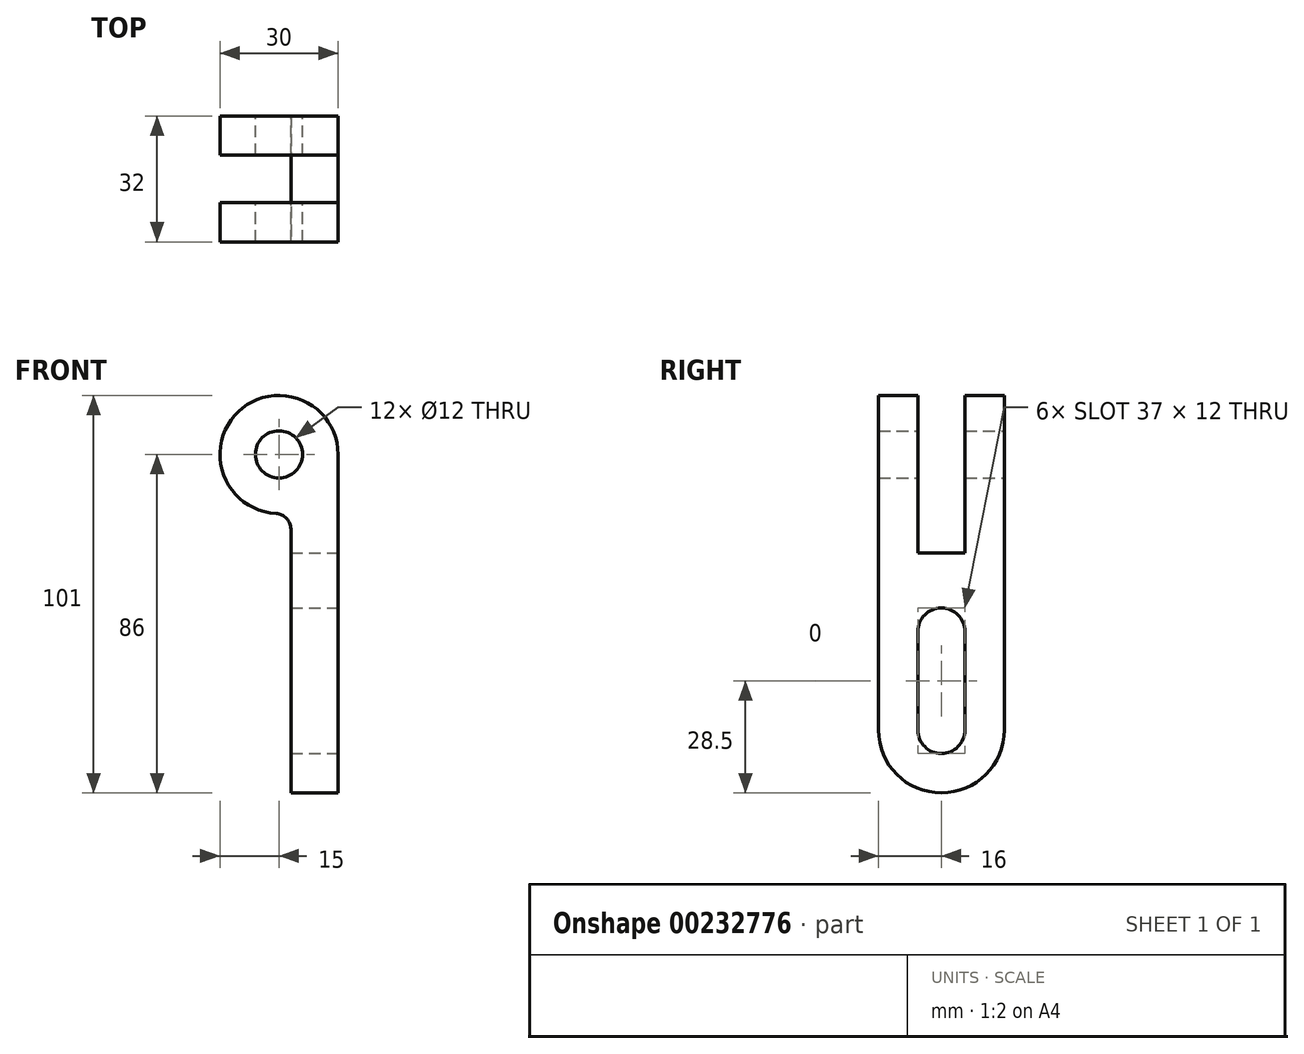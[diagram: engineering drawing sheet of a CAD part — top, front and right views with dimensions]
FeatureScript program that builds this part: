
annotation { "Feature Type Name" : "Feature", "Feature Type Description" : "" }
export const myFeature = defineFeature(function(context is Context, id is Id, definition is map)
    precondition{}
    {
        {
            var Q0;
            Q0=qCreatedBy(makeId("Front.planeOp"),FACE);
            var sketch = newSketch(context, id + "F0", { "sketchPlane" : qUnion([Q0])});
            skArc(sketch, "E0", {"start": v(15, 0) * mm, "mid": v(-10.32, 10.88) * mm, "end": v(-0.79, -14.98) * mm});
            skCircle(sketch, "E1", {"center": v(0, 0) * mm, "radius": 6 * mm});
            skLineSegment(sketch, "E2", {"start": v(15, 0) * mm, "end": v(15, -86) * mm});
            skLineSegment(sketch, "E3", {"start": v(15, -86) * mm, "end": v(3, -86) * mm});
            skLineSegment(sketch, "E4", {"start": v(3, -86) * mm, "end": v(3, -18.97) * mm});
            skPoint(sketch, "E5.visualSharp", {"position": v(3, -14.7) * mm});
            skArc(sketch, "E5.filletArc", {"start": v(3, -18.97) * mm, "mid": v(1.9, -16.22) * mm, "end": v(-0.79, -14.98) * mm});
            skSolve(sketch);
        }
        {
            var Q0;
            Q0 = qSketchRegion(id + "F0", true);
            extrude(context, id + "F1", {"entities" : qUnion([Q0]), "depth" : 32 * mm});
        }
        {
            var Q0;
            Q0=makeQuery(id+"F1.opExtrude","SWEPT_FACE",FACE,{"disambiguationData":[OSD([sQuery(id+"F0.wireOp",EDGE,"E2")])]});
            var sketch = newSketch(context, id + "F2", { "sketchPlane" : qUnion([Q0])});
            skLineSegment(sketch, "E6.0.0", {"start": v(0, -86) * mm, "end": v(0, -70) * mm, "construction": true});
            skLineSegment(sketch, "E6.0.1", {"start": v(0, 0) * mm, "end": v(-32, 0) * mm, "construction": true});
            skLineSegment(sketch, "E6.0.2", {"start": v(-32, 0) * mm, "end": v(-32, -61) * mm, "construction": true});
            skLineSegment(sketch, "E6.0.3", {"start": v(-32, -86) * mm, "end": v(0, -86) * mm, "construction": true});
            skLineSegment(sketch, "E7", {"start": v(-32, 15) * mm, "end": v(0, 15) * mm, "construction": true});
            skLineSegment(sketch, "E8.bottom", {"start": v(-22, 15) * mm, "end": v(-10, 15) * mm});
            skLineSegment(sketch, "E8.top", {"start": v(-22, -25) * mm, "end": v(-10, -25) * mm});
            skLineSegment(sketch, "E8.left", {"start": v(-22, 15) * mm, "end": v(-22, -25) * mm});
            skLineSegment(sketch, "E8.right", {"start": v(-10, 15) * mm, "end": v(-10, -25) * mm});
            skArc(sketch, "E9", {"start": v(-32, -70) * mm, "mid": v(-16, -86) * mm, "end": v(0, -70) * mm});
            skLineSegment(sketch, "E10", {"start": v(-32, -86) * mm, "end": v(0, -86) * mm});
            skLineSegment(sketch, "E11", {"start": v(-32, -86) * mm, "end": v(-32, -70) * mm});
            skLineSegment(sketch, "E12", {"start": v(0, -86) * mm, "end": v(0, -70) * mm});
            skLineSegment(sketch, "E13.trimOffspring", {"start": v(-32, -70) * mm, "end": v(-32, -86) * mm, "construction": true});
            skLineSegment(sketch, "E14.trimOffspring", {"start": v(0, -57.7) * mm, "end": v(0, 0) * mm, "construction": true});
            skLineSegment(sketch, "E15.0.0", {"start": v(0, -86) * mm, "end": v(0, 0) * mm, "construction": true});
            skLineSegment(sketch, "E15.0.2", {"start": v(-32, 0) * mm, "end": v(-32, -86) * mm, "construction": true});
            skArc(sketch, "E16", {"start": v(-22, -70) * mm, "mid": v(-16, -76) * mm, "end": v(-10, -70) * mm});
            skArc(sketch, "E17", {"start": v(-10, -45) * mm, "mid": v(-16, -39) * mm, "end": v(-22, -45) * mm});
            skLineSegment(sketch, "E18", {"start": v(-10, -45) * mm, "end": v(-10, -70) * mm});
            skLineSegment(sketch, "E19", {"start": v(-22, -45) * mm, "end": v(-22, -70) * mm});
            skSolve(sketch);
        }
        {
            var Q0;
            Q0=makeQuery(id+"F2.imprint","IMPRINT",FACE,{"disambiguationData":[TD([[makeQuery(id+"F2.imprint","IMPRINT",EDGE,{"derivedFrom":sQuery(id+"F2.wireOp",EDGE,"E16")}),1.0]])]});
            var Q1;
            {var subQ0=sQuery(id+"F2.wireOp",EDGE,"E8.top");Q1=makeQuery(id+"F2.imprint","IMPRINT",FACE,{"disambiguationData":[TD([[makeQuery(id+"F2.imprint","IMPRINT",EDGE,{"derivedFrom":subQ0}),1.0]])]});}
            var Q2;
            {var subQ0=sQuery(id+"F2.wireOp",EDGE,"E11");Q2=makeQuery(id+"F2.imprint","IMPRINT",FACE,{"disambiguationData":[TD([[makeQuery(id+"F2.imprint","IMPRINT",EDGE,{"derivedFrom":subQ0}),1.0]])]});}
            var Q3;
            {var subQ0=sQuery(id+"F2.wireOp",EDGE,"E12");Q3=makeQuery(id+"F2.imprint","IMPRINT",FACE,{"disambiguationData":[TD([[makeQuery(id+"F2.imprint","IMPRINT",EDGE,{"derivedFrom":subQ0}),-1.0]])]});}
            var Q4;
            {var subQ0=sQuery(id+"F2.wireOp",EDGE,"E8.bottom");Q4=makeQuery(id+"F2.imprint","IMPRINT",FACE,{"disambiguationData":[TD([[makeQuery(id+"F2.imprint","IMPRINT",EDGE,{"derivedFrom":subQ0}),-1.0]])]});}
            extrude(context, id + "F3", {"entities" : qUnion([Q0, Q1, Q2, Q3, Q4]), "operationType" : NewBodyOperationType.REMOVE, "endBound" : BoundingType.THROUGH_ALL, "oppositeDirection" : true, "depth" : 25 * mm});
        }
    });
